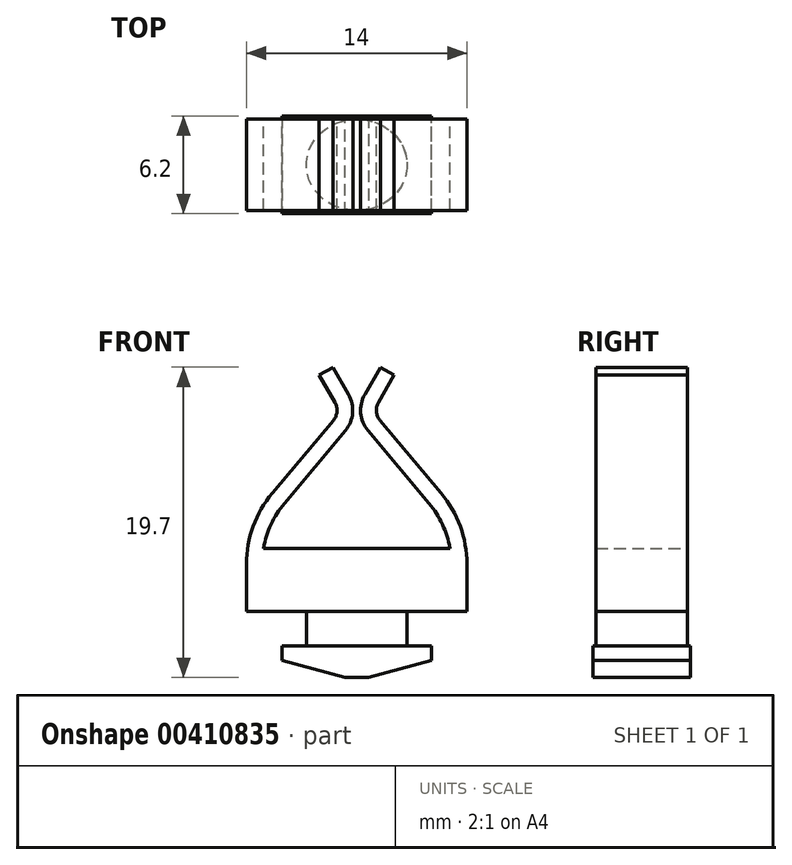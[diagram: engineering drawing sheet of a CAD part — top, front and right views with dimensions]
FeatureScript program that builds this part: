
annotation { "Feature Type Name" : "Feature", "Feature Type Description" : "" }
export const myFeature = defineFeature(function(context is Context, id is Id, definition is map)
    precondition{}
    {
        {
            var Q0;
            Q0=qCreatedBy(makeId("Front.planeOp"),FACE);
            var sketch = newSketch(context, id + "F0", { "sketchPlane" : qUnion([Q0])});
            skLineSegment(sketch, "E0.bottom", {"start": v(-7, 3) * mm, "end": v(7, 3) * mm});
            skLineSegment(sketch, "E0.top", {"start": v(-7, 0) * mm, "end": v(7, 0) * mm});
            skLineSegment(sketch, "E0.left", {"start": v(-7, 3) * mm, "end": v(-7, 0) * mm});
            skLineSegment(sketch, "E0.right", {"start": v(7, 3) * mm, "end": v(7, 0) * mm});
            skSolve(sketch);
        }
        {
            var Q0;
            Q0=qSketchRegion(id+"F0",true);
            extrude(context, id + "F1", {"entities" : qUnion([Q0]), "endBound" : BoundingType.SYMMETRIC, "depth" : 5.8 * mm});
        }
        {
            var Q0;
            Q0=makeQuery(id+"F1.opExtrude","SWEPT_FACE",FACE,{"disambiguationData":[OSD([sQuery(id+"F0.wireOp",EDGE,"E0.top")])]});
            var sketch = newSketch(context, id + "F2", { "sketchPlane" : qUnion([Q0])});
            skEllipse(sketch, "E1", {"center": v(0, 0) * mm, "majorRadius": 3.2 * mm, "minorRadius": 2.9 * mm, "majorAxis": v(1, 0)});
            skSolve(sketch);
        }
        {
            var Q0;
            Q0=qSketchRegion(id+"F2",true);
            extrude(context, id + "F3", {"entities" : qUnion([Q0]), "operationType" : NewBodyOperationType.ADD, "depth" : 2.2 * mm});
        }
        {
            var Q0;
            Q0=qCreatedBy(makeId("Front.planeOp"),FACE);
            var sketch = newSketch(context, id + "F4", { "sketchPlane" : qUnion([Q0])});
            skLineSegment(sketch, "E2.bottom", {"start": v(-4.75, -2.2) * mm, "end": v(4.75, -2.2) * mm});
            skLineSegment(sketch, "E2.top", {"start": v(-4.75, -4.2) * mm, "end": v(4.75, -4.2) * mm});
            skLineSegment(sketch, "E2.left", {"start": v(-4.75, -2.2) * mm, "end": v(-4.75, -4.2) * mm});
            skLineSegment(sketch, "E2.right", {"start": v(4.75, -2.2) * mm, "end": v(4.75, -4.2) * mm});
            skPoint(sketch, "E3", {"position": v(0, -2.2) * mm});
            skSolve(sketch);
        }
        {
            var Q0;
            Q0=makeQuery(id+"F4.imprint","IMPRINT",FACE,{"disambiguationData":[TD([[makeQuery(id+"F4.imprint","IMPRINT",EDGE,{"derivedFrom":sQuery(id+"F4.wireOp",EDGE,"E2.bottom")}),-1.0]])]});
            extrude(context, id + "F5", {"entities" : qUnion([Q0]), "operationType" : NewBodyOperationType.ADD, "endBound" : BoundingType.SYMMETRIC, "depth" : 6.2 * mm});
        }
        {
            var Q0;
            Q0=makeQuery(id+"F5.opExtrude","SWEPT_EDGE",EDGE,{"disambiguationData":[OSD([sQuery(id+"F4.wireOp",EDGE,"E2.top"),sQuery(id+"F4.wireOp",EDGE,"E2.right")])]});
            var Q1;
            Q1=makeQuery(id+"F5.opExtrude","SWEPT_EDGE",EDGE,{"disambiguationData":[OSD([sQuery(id+"F4.wireOp",EDGE,"E2.top"),sQuery(id+"F4.wireOp",EDGE,"E2.left")])]});
            chamfer(context, id + "F6", {"entities" : qUnion([Q0, Q1]), "chamferType" : ChamferType.OFFSET_ANGLE, "width" : 4 * mm, "oppositeDirection" : true, "angle" : 15 * degree, "tangentPropagation" : true});
        }
        {
            var Q0;
            Q0=qCreatedBy(makeId("Front.planeOp"),FACE);
            var sketch = newSketch(context, id + "F7", { "sketchPlane" : qUnion([Q0])});
            skArc(sketch, "E4", {"start": v(7, 3) * mm, "mid": v(6.58, 5.4) * mm, "end": v(5.36, 7.5) * mm});
            skLineSegment(sketch, "E5.0", {"start": v(-7, 3) * mm, "end": v(7, 3) * mm});
            skLineSegment(sketch, "E6", {"start": v(-5.36, 7.5) * mm, "end": v(-1.48, 12.12) * mm});
            skLineSegment(sketch, "E7", {"start": v(0, 3) * mm, "end": v(0, 11.65) * mm, "construction": true});
            skLineSegment(sketch, "E8.MirrorCS", {"start": v(5.36, 7.5) * mm, "end": v(1.48, 12.12) * mm});
            skArc(sketch, "E9", {"start": v(1.48, 12.12) * mm, "mid": v(1.25, 12.68) * mm, "end": v(1.38, 13.26) * mm});
            skLineSegment(sketch, "E10", {"start": v(1.38, 13.26) * mm, "end": v(2.38, 15) * mm});
            skArc(sketch, "E11.MirrorCS", {"start": v(-1.48, 12.12) * mm, "mid": v(-1.25, 12.68) * mm, "end": v(-1.38, 13.26) * mm});
            skLineSegment(sketch, "E12.MirrorCS", {"start": v(-1.38, 13.26) * mm, "end": v(-2.38, 15) * mm});
            skArc(sketch, "E13.trimOffspring", {"start": v(-5.36, 7.5) * mm, "mid": v(-6.58, 5.4) * mm, "end": v(-7, 3) * mm});
            skLineSegment(sketch, "E14.0", {"start": v(-0.52, 13.76) * mm, "end": v(-1.52, 15.5) * mm});
            skArc(sketch, "E14.1", {"start": v(-0.72, 11.48) * mm, "mid": v(-0.26, 12.6) * mm, "end": v(-0.52, 13.76) * mm});
            skLineSegment(sketch, "E14.2", {"start": v(-4.6, 6.86) * mm, "end": v(-0.72, 11.48) * mm});
            skArc(sketch, "E14.3", {"start": v(-4.6, 6.86) * mm, "mid": v(-5.45, 5.52) * mm, "end": v(-5.92, 4) * mm});
            skLineSegment(sketch, "E14.4", {"start": v(-5.92, 4) * mm, "end": v(5.92, 4) * mm});
            skLineSegment(sketch, "E14.5", {"start": v(0.52, 13.76) * mm, "end": v(1.52, 15.5) * mm});
            skArc(sketch, "E14.6", {"start": v(0.72, 11.48) * mm, "mid": v(0.26, 12.6) * mm, "end": v(0.52, 13.76) * mm});
            skLineSegment(sketch, "E14.7", {"start": v(4.6, 6.86) * mm, "end": v(0.72, 11.48) * mm});
            skArc(sketch, "E14.8", {"start": v(5.92, 4) * mm, "mid": v(5.45, 5.52) * mm, "end": v(4.6, 6.86) * mm});
            skLineSegment(sketch, "E15", {"start": v(-2.38, 15) * mm, "end": v(-1.52, 15.5) * mm});
            skLineSegment(sketch, "E16", {"start": v(1.52, 15.5) * mm, "end": v(2.38, 15) * mm});
            skSolve(sketch);
        }
        {
            var Q0;
            Q0=qSketchRegion(id+"F7",true);
            extrude(context, id + "F8", {"entities" : qUnion([Q0]), "operationType" : NewBodyOperationType.ADD, "endBound" : BoundingType.SYMMETRIC, "depth" : 5.8 * mm});
        }
    });
